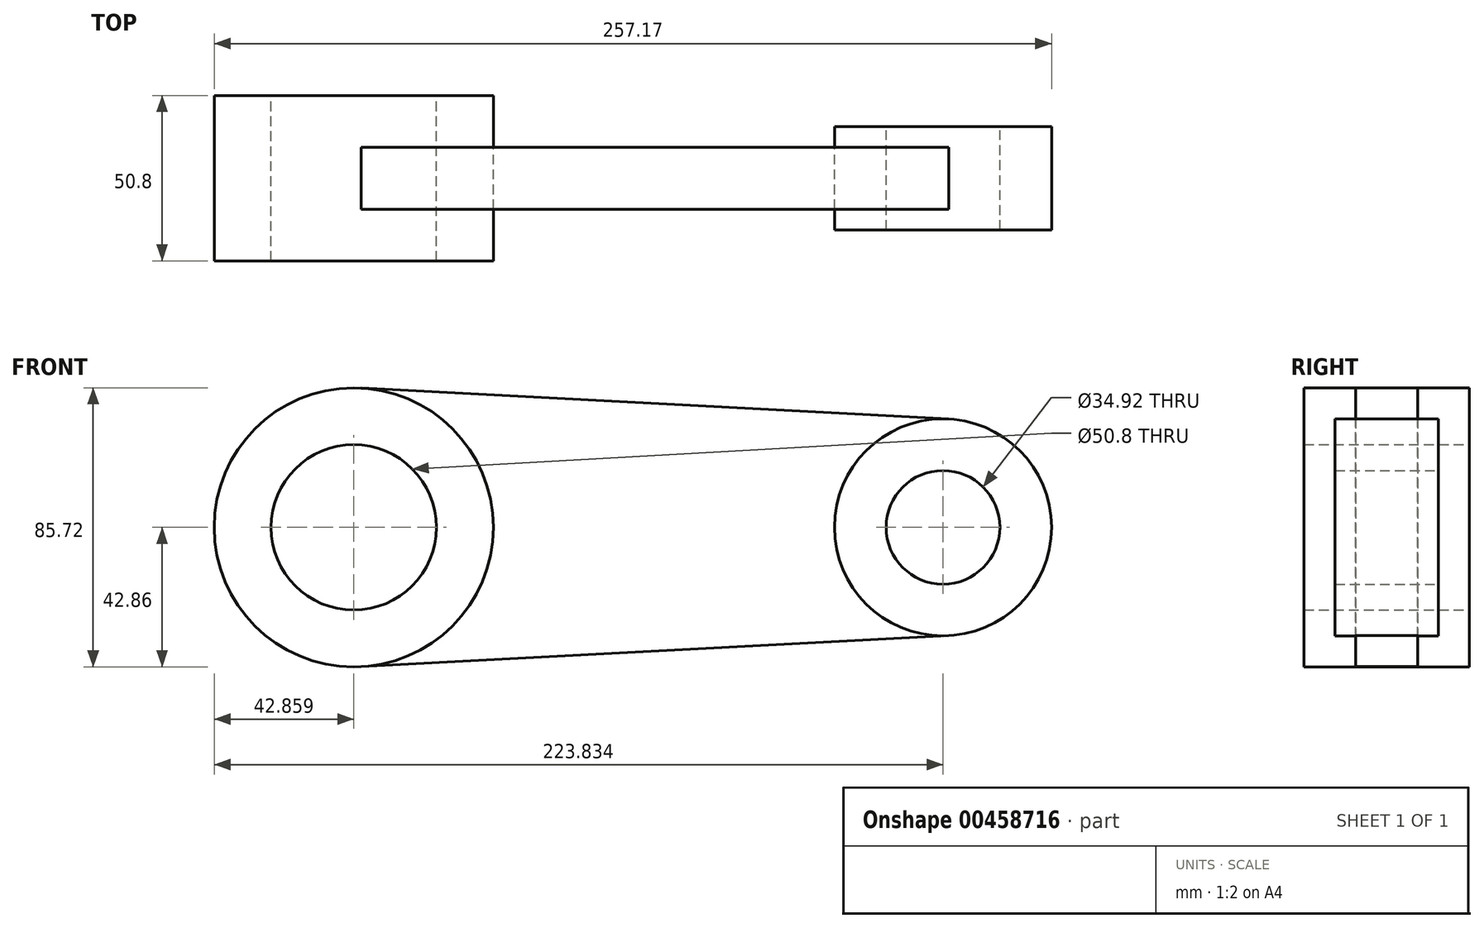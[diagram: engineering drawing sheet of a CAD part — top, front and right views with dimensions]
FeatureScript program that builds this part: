
annotation { "Feature Type Name" : "Feature", "Feature Type Description" : "" }
export const myFeature = defineFeature(function(context is Context, id is Id, definition is map)
    precondition{}
    {
        {
            var Q0;
            Q0=qCreatedBy(makeId("Front.planeOp"),FACE);
            var sketch = newSketch(context, id + "F0", { "sketchPlane" : qUnion([Q0])});
            skCircle(sketch, "E0", {"center": v(-135.67, 0) * mm, "radius": 25.4 * mm});
            skCircle(sketch, "E1", {"center": v(-135.67, 0) * mm, "radius": 42.86 * mm});
            skCircle(sketch, "E2", {"center": v(45.3, 0) * mm, "radius": 17.46 * mm});
            skCircle(sketch, "E3", {"center": v(45.3, 0) * mm, "radius": 33.34 * mm});
            skLineSegment(sketch, "E4", {"start": v(-133.42, -42.8) * mm, "end": v(47.06, -33.3) * mm});
            skLineSegment(sketch, "E5", {"start": v(-133.42, 42.8) * mm, "end": v(47.06, 33.3) * mm});
            skSolve(sketch);
        }
        {
            var Q0;
            {var subQ0=sQuery(id+"F0.wireOp",EDGE,"RluNvbC4-Xolj-I1dp-g8KM-tY4VAqvq9iQ1");var subQ1=sQuery(id+"F0.wireOp",EDGE,"E1");var subQ2=makeQuery(id+"F0.imprint","INTERSECT",VERTEX,{"disambiguationData":[OD(0.0)],"derivedFrom":[subQ1,subQ0]});Q0=makeQuery(id+"F0.imprint","IMPRINT",FACE,{"disambiguationData":[TD([[makeQuery(id+"F0.imprint","IMPRINT",EDGE,{"disambiguationData":[TD([[subQ2,1.0]])],"derivedFrom":subQ1}),1.0]])]});}
            var Q1;
            {var subQ0=sQuery(id+"F0.wireOp",EDGE,"NJSf5rRz-06eI-PsMK-ZbyU-XNEEseMUXoM8");var subQ1=sQuery(id+"F0.wireOp",EDGE,"E1");var subQ2=makeQuery(id+"F0.imprint","INTERSECT",VERTEX,{"disambiguationData":[OD(0.0)],"derivedFrom":[subQ1,subQ0]});Q1=makeQuery(id+"F0.imprint","IMPRINT",FACE,{"disambiguationData":[TD([[makeQuery(id+"F0.imprint","IMPRINT",EDGE,{"disambiguationData":[TD([[subQ2,-1.0]])],"derivedFrom":subQ1}),1.0]])]});}
            var Q2;
            Q2=makeQuery(id+"F0.imprint","IMPRINT",FACE,{"disambiguationData":[TD([[makeQuery(id+"F0.imprint","IMPRINT",EDGE,{"derivedFrom":sQuery(id+"F0.wireOp",EDGE,"E0")}),-1.0]])]});
            extrude(context, id + "F1", {"entities" : qUnion([Q0, Q1, Q2]), "depth" : 50.8 * mm, "symmetric" : true});
        }
        {
            var Q0;
            Q0=makeQuery(id+"F0.imprint","IMPRINT",FACE,{"disambiguationData":[TD([[makeQuery(id+"F0.imprint","IMPRINT",EDGE,{"derivedFrom":sQuery(id+"F0.wireOp",EDGE,"E2")}),-1.0]])]});
            extrude(context, id + "F2", {"entities" : qUnion([Q0]), "depth" : 31.75 * mm, "symmetric" : true});
        }
        {
            var Q0;
            {var subQ0=sQuery(id+"F0.wireOp",EDGE,"E4");var subQ1=sQuery(id+"F0.wireOp",EDGE,"E1");var subQ2=makeQuery(id+"F0.imprint","INTERSECT",VERTEX,{"derivedFrom":[subQ1,subQ0]});Q0=makeQuery(id+"F0.imprint","IMPRINT",FACE,{"disambiguationData":[TD([[makeQuery(id+"F0.imprint","IMPRINT",EDGE,{"disambiguationData":[TD([[subQ2,-1.0]])],"derivedFrom":subQ1}),-1.0]])]});}
            extrude(context, id + "F3", {"entities" : qUnion([Q0]), "depth" : 19.05 * mm, "symmetric" : true});
        }
    });
